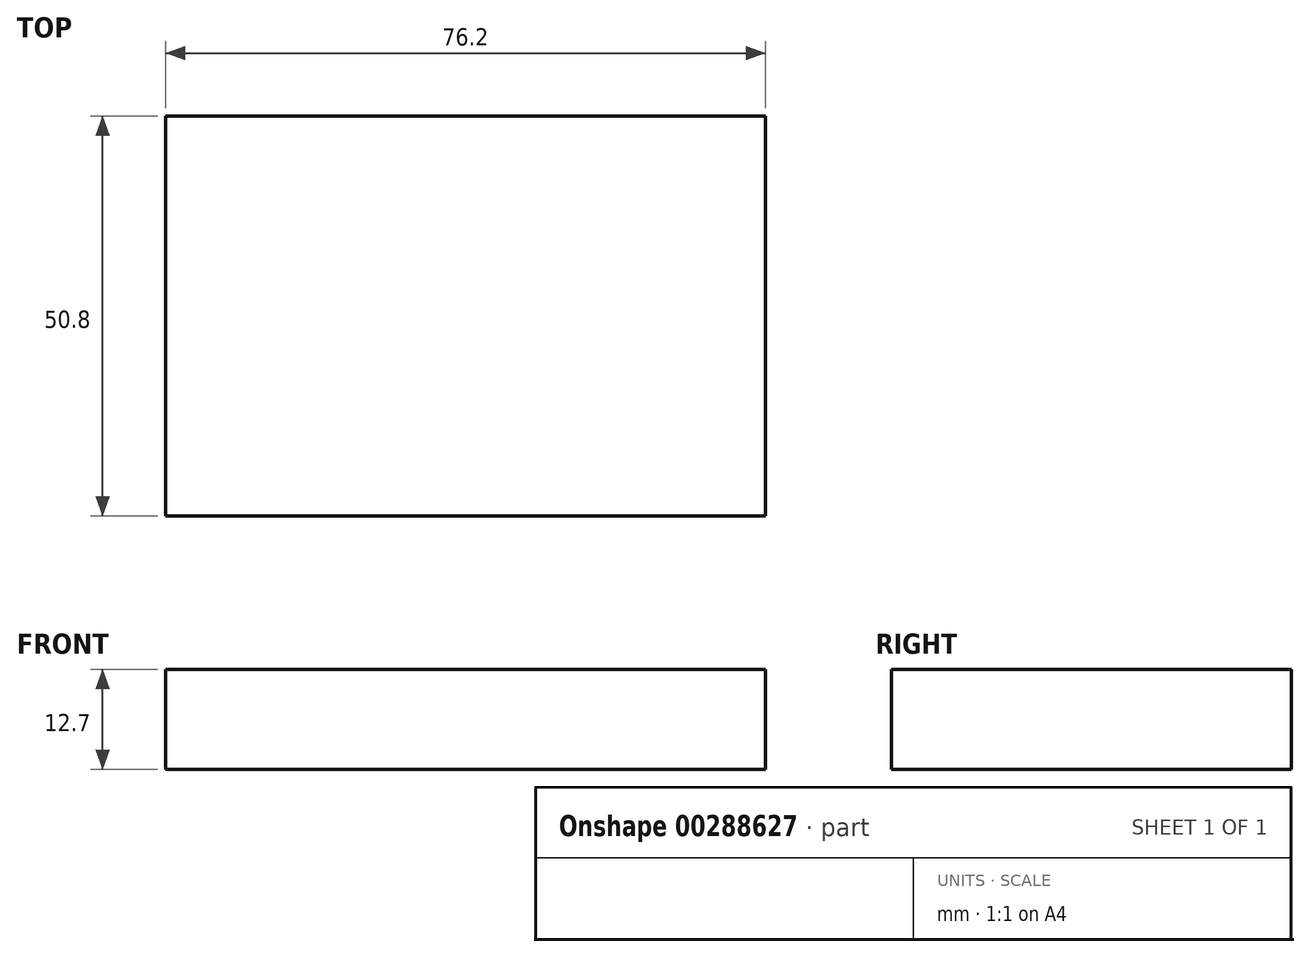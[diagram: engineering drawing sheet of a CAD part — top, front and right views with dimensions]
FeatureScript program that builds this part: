
annotation { "Feature Type Name" : "Feature", "Feature Type Description" : "" }
export const myFeature = defineFeature(function(context is Context, id is Id, definition is map)
    precondition{}
    {
        {
            var Q0;
            Q0=qCreatedBy(makeId("Front.planeOp"),FACE);
            var sketch = newSketch(context, id + "F0", { "sketchPlane" : qUnion([Q0])});
            skLineSegment(sketch, "E0", {"start": v(0, 0) * mm, "end": v(0, 12.7) * mm});
            skLineSegment(sketch, "E1", {"start": v(0, 12.7) * mm, "end": v(76.2, 12.7) * mm});
            skLineSegment(sketch, "E2", {"start": v(76.2, 12.7) * mm, "end": v(76.2, 0) * mm});
            skLineSegment(sketch, "E3", {"start": v(76.2, 0) * mm, "end": v(0, 0) * mm});
            skSolve(sketch);
        }
        {
            var Q0;
            Q0=makeQuery(id+"F0.imprint","IMPRINT",FACE,{"disambiguationData":[TD([[makeQuery(id+"F0.imprint","IMPRINT",EDGE,{"derivedFrom":sQuery(id+"F0.wireOp",EDGE,"E0")}),-1.0]])]});
            extrude(context, id + "F1", {"entities" : qUnion([Q0]), "depth" : 50.8 * mm, "offsetDistance" : 25.4 * mm});
        }
    });
